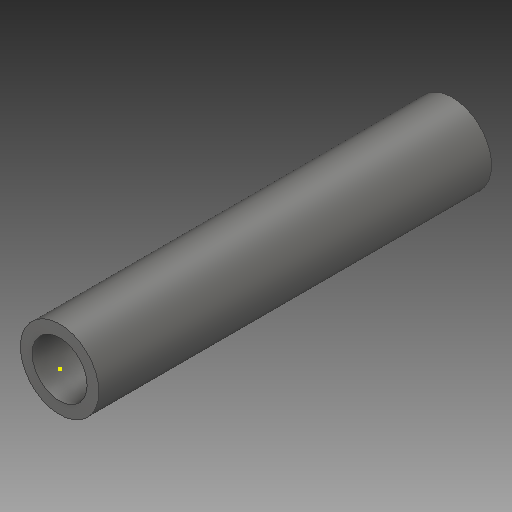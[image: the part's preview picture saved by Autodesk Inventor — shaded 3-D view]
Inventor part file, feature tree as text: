
AUTODESK INVENTOR PART (.ipt)
format: ipt  version: 2019 (Build 230136000, 136)  size: 107,520 bytes
history: native  units: mm
features: sketch x3, extrude x2
ambient origin geometry x8: Origin, YZ Plane, XZ Plane, XY Plane, X Axis, Y Axis, Z Axis, Center Point
bodies: Body1 (feature_tree)
feature tree (5):
  extrude  "Extrusion5"  Depth=500.0mm TaperAngle=0.0deg
  extrude  "Extrusion6"  Depth=500.0mm TaperAngle=0.0deg
  sketch  "Sketch7"
  sketch  "Sketch5"  dims[d12=100.0mm d13=500.0mm d14=0.0mm]
  sketch  "Sketch6"  dims[d15=70.0mm d16=500.0mm d17=0.0mm]
